# Revit family: Gira_200900
name_source: partatom
category: Allgemeines Modell
revit_build: Autodesk Revit 2017 (Build: 20160225_1515(x64)
units: mm (PartAtom-declared; Revit-internal decimal feet)

## family parameters
Basisbauteil = Fläche
Beim Laden mit Abzugskörper schneiden = Nein
Bemaßung runder Anschluss = Durchmesser verwenden
Gemeinsam genutzt = Nein
Kann Basisbauteil für Bewehrung sein = Nein
Raumberechnungspunkt = Nein
Teiletyp = Normal

## types (1)
- Gira_200900
    Andere Bussysteme = ohne
    BIM = https://media.stage.bim.site ext.Fühler KNX.rfa
    Befestigungsart = Krallen-/Schraubbefestigung
    Beschreibung = Einsatz KNX Busankoppler 3 mit externem Fühler   Merkmale: - Der Busankoppler 3 stellt die Verbindung zwischen dem KNX System und einem KNX Anwendungsmodul her. - Die Kombination aus dem Busankoppler 3 und einem Anwendungsmodul ergibt eine funktionale Einheit. - Im ETS-Projekt wird diese Einheit in Form des Applikationsprogramms des Anwendungsmoduls projektiert. - Am Busankoppler 3 mit externem Fühler kann zusätzlich ein Temperaturfernfühler angeschlossen werden. Ein Raumtemperaturregler kann dadurch die Temperatur an einer zusätzlichen Messstelle aufnehmen.  Hinweise : - Der Fernfühler funktioniert nur in Kombination mit einem Tastsensor 3 Plus.
    Bussystem Funkbus = Nein
    Bussystem KNX = Ja
    Bussystem KNX-Funk = Nein
    Bussystem LON = Nein
    Bussystem Powernet = Nein
    Datenblatt = https://katalog.gira.de
    GTIN = 4010337082194
    HAN = 200900
    Hersteller = Gira
    Montageart = Unterputz
    Produktseite = http://katalog.gira.de
    Typname = Busankoppler 3 externer Fühler KNX Einsatz
    URL = https://www.gira.de
    Vorgabe-Ansicht = 1219 mm

## geometry (parser evidence)
native form markers: Sweep x2
no freeform markers — native parametric forms only
